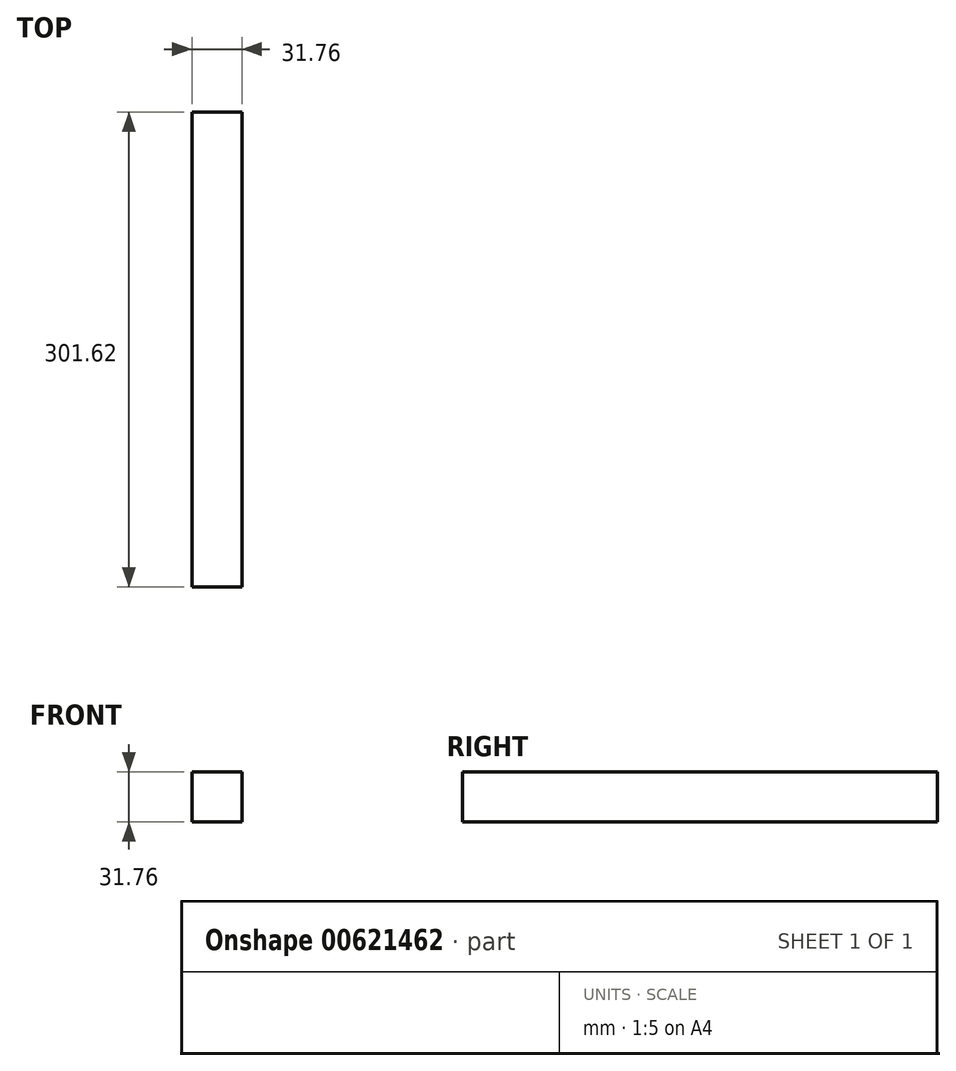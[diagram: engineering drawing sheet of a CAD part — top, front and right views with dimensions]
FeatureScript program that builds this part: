
annotation { "Feature Type Name" : "Feature", "Feature Type Description" : "" }
export const myFeature = defineFeature(function(context is Context, id is Id, definition is map)
    precondition{}
    {
        {
            var Q0;
            Q0=qCreatedBy(makeId("Front.planeOp"),FACE);
            var sketch = newSketch(context, id + "F0", { "sketchPlane" : qUnion([Q0])});
            skLineSegment(sketch, "E0.bottom", {"start": v(15.88, 15.88) * mm, "end": v(-15.88, 15.88) * mm});
            skLineSegment(sketch, "E0.top", {"start": v(15.88, -15.88) * mm, "end": v(-15.88, -15.88) * mm});
            skLineSegment(sketch, "E0.left", {"start": v(15.88, 15.88) * mm, "end": v(15.88, -15.88) * mm});
            skLineSegment(sketch, "E0.right", {"start": v(-15.88, 15.88) * mm, "end": v(-15.88, -15.88) * mm});
            skPoint(sketch, "E0.middle", {"position": v(0, 0) * mm});
            skSolve(sketch);
        }
        {
            var Q0;
            Q0 = qSketchRegion(id + "F0", true);
            extrude(context, id + "F1", {"entities" : qUnion([Q0]), "oppositeDirection" : true, "depth" : 301.62 * mm, "offsetDistance" : 25.4 * mm});
        }
    });
